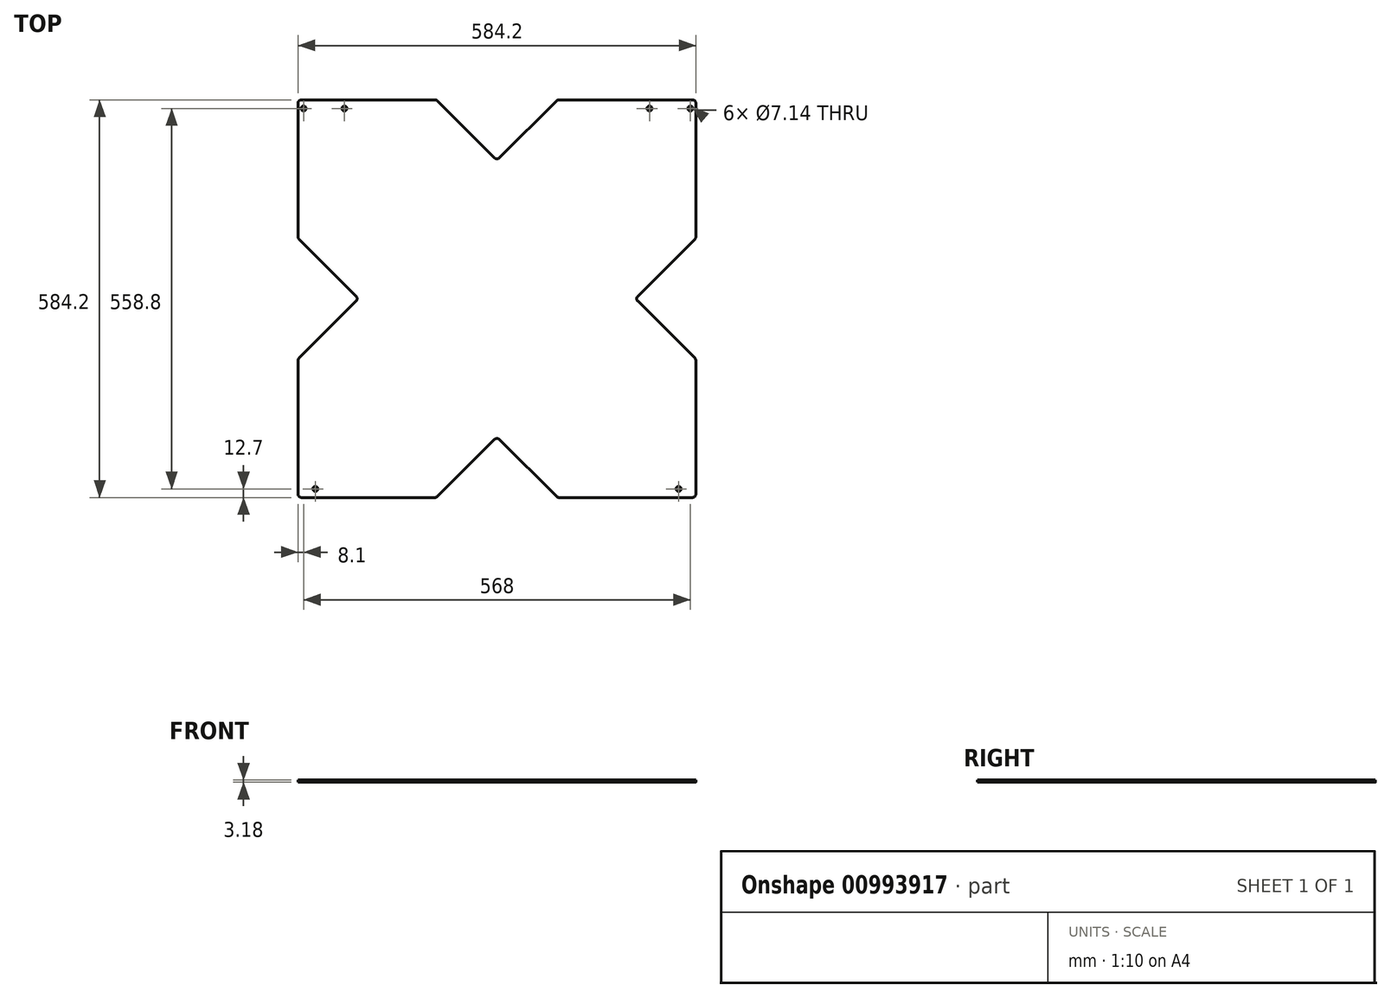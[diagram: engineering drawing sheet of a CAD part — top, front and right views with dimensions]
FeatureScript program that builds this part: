
annotation { "Feature Type Name" : "Feature", "Feature Type Description" : "" }
export const myFeature = defineFeature(function(context is Context, id is Id, definition is map)
    precondition{}
    {
        {
            var Q0;
            Q0=qCreatedBy(makeId("Top.planeOp"),FACE);
            var sketch = newSketch(context, id + "F0", { "sketchPlane" : qUnion([Q0])});
            skLineSegment(sketch, "E0.bottom", {"start": v(0, 0) * mm, "end": v(584.2, 0) * mm});
            skLineSegment(sketch, "E0.top", {"start": v(0, 584.2) * mm, "end": v(584.2, 584.2) * mm});
            skLineSegment(sketch, "E0.left", {"start": v(0, 0) * mm, "end": v(0, 584.2) * mm});
            skLineSegment(sketch, "E0.right", {"start": v(584.2, 0) * mm, "end": v(584.2, 584.2) * mm});
            skLineSegment(sketch, "E1", {"start": v(292.1, 584.2) * mm, "end": v(292.1, 0) * mm});
            skLineSegment(sketch, "E2", {"start": v(0, 292.1) * mm, "end": v(584.2, 292.1) * mm});
            skLineSegment(sketch, "E3", {"start": v(203.2, 584.2) * mm, "end": v(292.1, 495.3) * mm});
            skLineSegment(sketch, "E4", {"start": v(292.1, 495.3) * mm, "end": v(381, 584.2) * mm});
            skLineSegment(sketch, "E5.MirrorCS", {"start": v(203.2, 0) * mm, "end": v(292.1, 88.9) * mm});
            skLineSegment(sketch, "E6.MirrorCS", {"start": v(292.1, 88.9) * mm, "end": v(381, 0) * mm});
            skLineSegment(sketch, "E7", {"start": v(0, 381) * mm, "end": v(88.9, 292.1) * mm});
            skLineSegment(sketch, "E8", {"start": v(88.9, 292.1) * mm, "end": v(0, 203.2) * mm});
            skLineSegment(sketch, "E9.MirrorCS", {"start": v(584.2, 381) * mm, "end": v(495.3, 292.1) * mm});
            skLineSegment(sketch, "E10.MirrorCS", {"start": v(495.3, 292.1) * mm, "end": v(584.2, 203.2) * mm});
            skLineSegment(sketch, "E11.bottom", {"start": v(0, 584.2) * mm, "end": v(76.2, 584.2) * mm});
            skLineSegment(sketch, "E11.top", {"start": v(0, 614.68) * mm, "end": v(76.2, 614.68) * mm});
            skLineSegment(sketch, "E11.left", {"start": v(0, 584.2) * mm, "end": v(0, 614.68) * mm});
            skLineSegment(sketch, "E11.right", {"start": v(76.2, 584.2) * mm, "end": v(76.2, 614.68) * mm});
            skLineSegment(sketch, "E12.bottom", {"start": v(584.2, 584.2) * mm, "end": v(508, 584.2) * mm});
            skLineSegment(sketch, "E12.top", {"start": v(584.2, 614.68) * mm, "end": v(508, 614.68) * mm});
            skLineSegment(sketch, "E12.left", {"start": v(584.2, 584.2) * mm, "end": v(584.2, 614.68) * mm});
            skLineSegment(sketch, "E12.right", {"start": v(508, 584.2) * mm, "end": v(508, 614.68) * mm});
            skLineSegment(sketch, "E13", {"start": v(38.1, 614.68) * mm, "end": v(38.1, 584.2) * mm});
            skLineSegment(sketch, "E14", {"start": v(76.2, 599.44) * mm, "end": v(0, 599.44) * mm});
            skCircle(sketch, "E15", {"center": v(68.1, 599.44) * mm, "radius": 3.18 * mm});
            skCircle(sketch, "E16", {"center": v(8.1, 599.44) * mm, "radius": 3.15 * mm});
            skLineSegment(sketch, "E17", {"start": v(508, 599.44) * mm, "end": v(584.2, 599.44) * mm});
            skLineSegment(sketch, "E18", {"start": v(546.1, 614.68) * mm, "end": v(546.1, 584.2) * mm});
            skCircle(sketch, "E19", {"center": v(516.1, 599.44) * mm, "radius": 3.18 * mm});
            skCircle(sketch, "E20", {"center": v(576.1, 599.44) * mm, "radius": 3.18 * mm});
            skPoint(sketch, "E21", {"position": v(8.1, 571.5) * mm});
            skPoint(sketch, "E22", {"position": v(68.1, 571.5) * mm});
            skLineSegment(sketch, "E23", {"start": v(38.1, 584.2) * mm, "end": v(38.1, 519.33) * mm});
            skPoint(sketch, "E24.MirrorP", {"position": v(516.1, 571.5) * mm});
            skPoint(sketch, "E25.MirrorP", {"position": v(576.1, 571.5) * mm});
            skSolve(sketch);
        }
        {
            var Q0;
            {var subQ0=sQuery(id+"F0.wireOp",EDGE,"E3");Q0=makeQuery(id+"F0.imprint","IMPRINT",FACE,{"disambiguationData":[TD([[makeQuery(id+"F0.imprint","IMPRINT",EDGE,{"derivedFrom":subQ0}),-1.0]])]});}
            var Q1;
            {var subQ7=sQuery(id+"F0.wireOp",EDGE,"E4");Q1=makeQuery(id+"F0.imprint","IMPRINT",FACE,{"disambiguationData":[TD([[makeQuery(id+"F0.imprint","IMPRINT",EDGE,{"derivedFrom":subQ7}),-1.0]])]});}
            var Q2;
            {var subQ4=sQuery(id+"F0.wireOp",EDGE,"E5.MirrorCS");Q2=makeQuery(id+"F0.imprint","IMPRINT",FACE,{"disambiguationData":[TD([[makeQuery(id+"F0.imprint","IMPRINT",EDGE,{"derivedFrom":subQ4}),1.0]])]});}
            var Q3;
            {var subQ7=sQuery(id+"F0.wireOp",EDGE,"E6.MirrorCS");Q3=makeQuery(id+"F0.imprint","IMPRINT",FACE,{"disambiguationData":[TD([[makeQuery(id+"F0.imprint","IMPRINT",EDGE,{"derivedFrom":subQ7}),1.0]])]});}
            extrude(context, id + "F1", {"entities" : qUnion([Q0, Q1, Q2, Q3]), "depth" : 3.17 * mm, "offsetDistance" : 25.4 * mm});
        }
        {
            var Q0;
            Q0=makeQuery(id+"F1.opExtrude","SWEPT_EDGE",EDGE,{"disambiguationData":[OSD([sQuery(id+"F0.wireOp",EDGE,"E0.left"),sQuery(id+"F0.wireOp",EDGE,"E8")])]});
            var Q1;
            Q1=makeQuery(id+"F1.opExtrude","SWEPT_EDGE",EDGE,{"disambiguationData":[OSD([sQuery(id+"F0.wireOp",EDGE,"E2"),sQuery(id+"F0.wireOp",EDGE,"E7"),sQuery(id+"F0.wireOp",EDGE,"E8")])]});
            var Q2;
            Q2=makeQuery(id+"F1.opExtrude","SWEPT_EDGE",EDGE,{"disambiguationData":[OSD([sQuery(id+"F0.wireOp",EDGE,"E0.left"),sQuery(id+"F0.wireOp",EDGE,"E7")])]});
            var Q3;
            Q3=makeQuery(id+"F1.opExtrude","SWEPT_EDGE",EDGE,{"disambiguationData":[OSD([sQuery(id+"F0.wireOp",EDGE,"E0.bottom"),sQuery(id+"F0.wireOp",EDGE,"E0.left")])]});
            var Q4;
            Q4=makeQuery(id+"F1.opExtrude","SWEPT_EDGE",EDGE,{"disambiguationData":[OSD([sQuery(id+"F0.wireOp",EDGE,"E0.bottom"),sQuery(id+"F0.wireOp",EDGE,"E5.MirrorCS")])]});
            var Q5;
            Q5=makeQuery(id+"F1.opExtrude","SWEPT_EDGE",EDGE,{"disambiguationData":[OSD([sQuery(id+"F0.wireOp",EDGE,"E1"),sQuery(id+"F0.wireOp",EDGE,"E5.MirrorCS"),sQuery(id+"F0.wireOp",EDGE,"E6.MirrorCS")])]});
            var Q6;
            Q6=makeQuery(id+"F1.opExtrude","SWEPT_EDGE",EDGE,{"disambiguationData":[OSD([sQuery(id+"F0.wireOp",EDGE,"E0.bottom"),sQuery(id+"F0.wireOp",EDGE,"E6.MirrorCS")])]});
            var Q7;
            Q7=makeQuery(id+"F1.opExtrude","SWEPT_EDGE",EDGE,{"disambiguationData":[OSD([sQuery(id+"F0.wireOp",EDGE,"E0.bottom"),sQuery(id+"F0.wireOp",EDGE,"E0.right")])]});
            var Q8;
            Q8=makeQuery(id+"F1.opExtrude","SWEPT_EDGE",EDGE,{"disambiguationData":[OSD([sQuery(id+"F0.wireOp",EDGE,"E0.right"),sQuery(id+"F0.wireOp",EDGE,"E10.MirrorCS")])]});
            var Q9;
            Q9=makeQuery(id+"F1.opExtrude","SWEPT_EDGE",EDGE,{"disambiguationData":[OSD([sQuery(id+"F0.wireOp",EDGE,"E2"),sQuery(id+"F0.wireOp",EDGE,"E9.MirrorCS"),sQuery(id+"F0.wireOp",EDGE,"E10.MirrorCS")])]});
            var Q10;
            Q10=makeQuery(id+"F1.opExtrude","SWEPT_EDGE",EDGE,{"disambiguationData":[OSD([sQuery(id+"F0.wireOp",EDGE,"E0.right"),sQuery(id+"F0.wireOp",EDGE,"E9.MirrorCS")])]});
            var Q11;
            Q11=makeQuery(id+"F1.opExtrude","SWEPT_EDGE",EDGE,{"disambiguationData":[OSD([sQuery(id+"F0.wireOp",EDGE,"E12.top"),sQuery(id+"F0.wireOp",EDGE,"E12.left")])]});
            var Q12;
            Q12=makeQuery(id+"F1.opExtrude","SWEPT_EDGE",EDGE,{"disambiguationData":[OSD([sQuery(id+"F0.wireOp",EDGE,"E12.top"),sQuery(id+"F0.wireOp",EDGE,"E12.right")])]});
            var Q13;
            Q13=makeQuery(id+"F1.opExtrude","SWEPT_EDGE",EDGE,{"disambiguationData":[OSD([sQuery(id+"F0.wireOp",EDGE,"E0.top"),sQuery(id+"F0.wireOp",EDGE,"E12.bottom"),sQuery(id+"F0.wireOp",EDGE,"E12.right")])]});
            var Q14;
            Q14=makeQuery(id+"F1.opExtrude","SWEPT_EDGE",EDGE,{"disambiguationData":[OSD([sQuery(id+"F0.wireOp",EDGE,"E0.top"),sQuery(id+"F0.wireOp",EDGE,"E4")])]});
            var Q15;
            Q15=makeQuery(id+"F1.opExtrude","SWEPT_EDGE",EDGE,{"disambiguationData":[OSD([sQuery(id+"F0.wireOp",EDGE,"E1"),sQuery(id+"F0.wireOp",EDGE,"E3"),sQuery(id+"F0.wireOp",EDGE,"E4")])]});
            var Q16;
            Q16=makeQuery(id+"F1.opExtrude","SWEPT_EDGE",EDGE,{"disambiguationData":[OSD([sQuery(id+"F0.wireOp",EDGE,"E0.top"),sQuery(id+"F0.wireOp",EDGE,"E3")])]});
            var Q17;
            Q17=makeQuery(id+"F1.opExtrude","SWEPT_EDGE",EDGE,{"disambiguationData":[OSD([sQuery(id+"F0.wireOp",EDGE,"E0.top"),sQuery(id+"F0.wireOp",EDGE,"E11.bottom"),sQuery(id+"F0.wireOp",EDGE,"E11.right")])]});
            var Q18;
            Q18=makeQuery(id+"F1.opExtrude","SWEPT_EDGE",EDGE,{"disambiguationData":[OSD([sQuery(id+"F0.wireOp",EDGE,"E11.top"),sQuery(id+"F0.wireOp",EDGE,"E11.right")])]});
            var Q19;
            Q19=makeQuery(id+"F1.opExtrude","SWEPT_EDGE",EDGE,{"disambiguationData":[OSD([sQuery(id+"F0.wireOp",EDGE,"E11.top"),sQuery(id+"F0.wireOp",EDGE,"E11.left")])]});
            fillet(context, id + "F2", {"entities" : qUnion([Q0, Q1, Q2, Q3, Q4, Q5, Q6, Q7, Q8, Q9, Q10, Q11, Q12, Q13, Q14, Q15, Q16, Q17, Q18, Q19]), "radius" : 5.08 * mm, "tangentPropagation" : true, "allowEdgeOverflow" : false});
        }
        {
            var Q0;
            Q0=makeQuery(id+"F1.opExtrude","CAP_FACE",FACE,{"disambiguationData":[OSD([sQuery(id+"F0.wireOp",EDGE,"E0.bottom"),sQuery(id+"F0.wireOp",EDGE,"E0.top"),sQuery(id+"F0.wireOp",EDGE,"E0.left"),sQuery(id+"F0.wireOp",EDGE,"E0.right"),sQuery(id+"F0.wireOp",EDGE,"E3"),sQuery(id+"F0.wireOp",EDGE,"E4"),sQuery(id+"F0.wireOp",EDGE,"E5.MirrorCS"),sQuery(id+"F0.wireOp",EDGE,"E6.MirrorCS"),sQuery(id+"F0.wireOp",EDGE,"E7"),sQuery(id+"F0.wireOp",EDGE,"E8"),sQuery(id+"F0.wireOp",EDGE,"E9.MirrorCS"),sQuery(id+"F0.wireOp",EDGE,"E10.MirrorCS"),sQuery(id+"F0.wireOp",EDGE,"E11.top"),sQuery(id+"F0.wireOp",EDGE,"E11.left"),sQuery(id+"F0.wireOp",EDGE,"E11.right"),sQuery(id+"F0.wireOp",EDGE,"E12.top"),sQuery(id+"F0.wireOp",EDGE,"E12.left"),sQuery(id+"F0.wireOp",EDGE,"E12.right"),sQuery(id+"F0.wireOp",EDGE,"E15"),sQuery(id+"F0.wireOp",EDGE,"E16"),sQuery(id+"F0.wireOp",EDGE,"E19"),sQuery(id+"F0.wireOp",EDGE,"E20")])],"isStart":false});
            var sketch = newSketch(context, id + "F3", { "sketchPlane" : qUnion([Q0])});
            skPoint(sketch, "E26", {"position": v(25.4, 12.7) * mm});
            skPoint(sketch, "E27", {"position": v(558.8, 12.7) * mm});
            skSolve(sketch);
        }
        {
            var Q0;
            Q0=sQuery(id+"F3.wireOp",VERTEX,"E26");
            var Q1;
            Q1=sQuery(id+"F3.wireOp",VERTEX,"E27");
            var Q2;
            Q2=sQuery(id+"F0.wireOp",VERTEX,"E21");
            var Q3;
            Q3=sQuery(id+"F0.wireOp",VERTEX,"E22");
            var Q4;
            Q4=sQuery(id+"F0.wireOp",VERTEX,"E24.MirrorP");
            var Q5;
            Q5=sQuery(id+"F0.wireOp",VERTEX,"E25.MirrorP");
            var Q6;
            Q6=makeQuery(id+"F1.opExtrude","SWEPT_BODY",BODY,{"disambiguationData":[OSD([sQuery(id+"F0.wireOp",EDGE,"E0.bottom"),sQuery(id+"F0.wireOp",EDGE,"E0.top"),sQuery(id+"F0.wireOp",EDGE,"E0.left"),sQuery(id+"F0.wireOp",EDGE,"E0.right"),sQuery(id+"F0.wireOp",EDGE,"E3"),sQuery(id+"F0.wireOp",EDGE,"E4"),sQuery(id+"F0.wireOp",EDGE,"E5.MirrorCS"),sQuery(id+"F0.wireOp",EDGE,"E6.MirrorCS"),sQuery(id+"F0.wireOp",EDGE,"E7"),sQuery(id+"F0.wireOp",EDGE,"E8"),sQuery(id+"F0.wireOp",EDGE,"E9.MirrorCS"),sQuery(id+"F0.wireOp",EDGE,"E10.MirrorCS"),sQuery(id+"F0.wireOp",EDGE,"E11.top"),sQuery(id+"F0.wireOp",EDGE,"E11.left"),sQuery(id+"F0.wireOp",EDGE,"E11.right"),sQuery(id+"F0.wireOp",EDGE,"E12.top"),sQuery(id+"F0.wireOp",EDGE,"E12.left"),sQuery(id+"F0.wireOp",EDGE,"E12.right"),sQuery(id+"F0.wireOp",EDGE,"E15"),sQuery(id+"F0.wireOp",EDGE,"E16"),sQuery(id+"F0.wireOp",EDGE,"E19"),sQuery(id+"F0.wireOp",EDGE,"E20")])]});
            hole(context, id + "F4", {"style" : HoleStyle.SIMPLE, "endStyle" : HoleEndStyle.THROUGH, "standardTappedOrClearance" : lookupTablePath({ "fit" : "Normal (ASME)", "standard" : "ANSI", "size" : "1/4", "type" : "Clearance" }), "standardBlindInLast" : lookupTablePath({ "fit" : "Normal", "standard" : "ANSI", "engagement" : "75%", "pitch" : "20 tpi", "size" : "1/4", "type" : "Clearance & tapped" }), "holeDiameter" : 7.14 * mm, "majorDiameter" : 6.35 * mm, "isTappedThrough" : true, "tappedDepth" : 12.7 * mm, "tapClearance" : 3, "locations" : qUnion([Q0, Q1, Q2, Q3, Q4, Q5]), "scope" : qUnion([Q6])});
        }
        {
            var Q0;
            Q0=sQuery(id+"F0.wireOp",VERTEX,"E21");
            var Q1;
            Q1=sQuery(id+"F0.wireOp",VERTEX,"E22");
            var Q2;
            Q2=sQuery(id+"F0.wireOp",VERTEX,"E24.MirrorP");
            var Q3;
            Q3=sQuery(id+"F0.wireOp",VERTEX,"E25.MirrorP");
            var Q4;
            Q4=makeQuery(id+"F1.opExtrude","SWEPT_BODY",BODY,{"disambiguationData":[OSD([sQuery(id+"F0.wireOp",EDGE,"E0.bottom"),sQuery(id+"F0.wireOp",EDGE,"E0.top"),sQuery(id+"F0.wireOp",EDGE,"E0.left"),sQuery(id+"F0.wireOp",EDGE,"E0.right"),sQuery(id+"F0.wireOp",EDGE,"E3"),sQuery(id+"F0.wireOp",EDGE,"E4"),sQuery(id+"F0.wireOp",EDGE,"E5.MirrorCS"),sQuery(id+"F0.wireOp",EDGE,"E6.MirrorCS"),sQuery(id+"F0.wireOp",EDGE,"E7"),sQuery(id+"F0.wireOp",EDGE,"E8"),sQuery(id+"F0.wireOp",EDGE,"E9.MirrorCS"),sQuery(id+"F0.wireOp",EDGE,"E10.MirrorCS"),sQuery(id+"F0.wireOp",EDGE,"E11.bottom"),sQuery(id+"F0.wireOp",EDGE,"E12.bottom")])]});
            hole(context, id + "F5", {"style" : HoleStyle.SIMPLE, "endStyle" : HoleEndStyle.THROUGH, "oppositeDirection" : true, "standardTappedOrClearance" : lookupTablePath({ "fit" : "Normal (ASME)", "standard" : "ANSI", "size" : "1/4", "type" : "Clearance" }), "standardBlindInLast" : lookupTablePath({ "fit" : "Normal", "standard" : "ANSI", "engagement" : "75%", "pitch" : "20 tpi", "size" : "1/4", "type" : "Clearance & tapped" }), "holeDiameter" : 7.14 * mm, "majorDiameter" : 6.35 * mm, "isTappedThrough" : true, "tappedDepth" : 12.7 * mm, "tapClearance" : 3, "locations" : qUnion([Q0, Q1, Q2, Q3]), "scope" : qUnion([Q4])});
        }
    });
